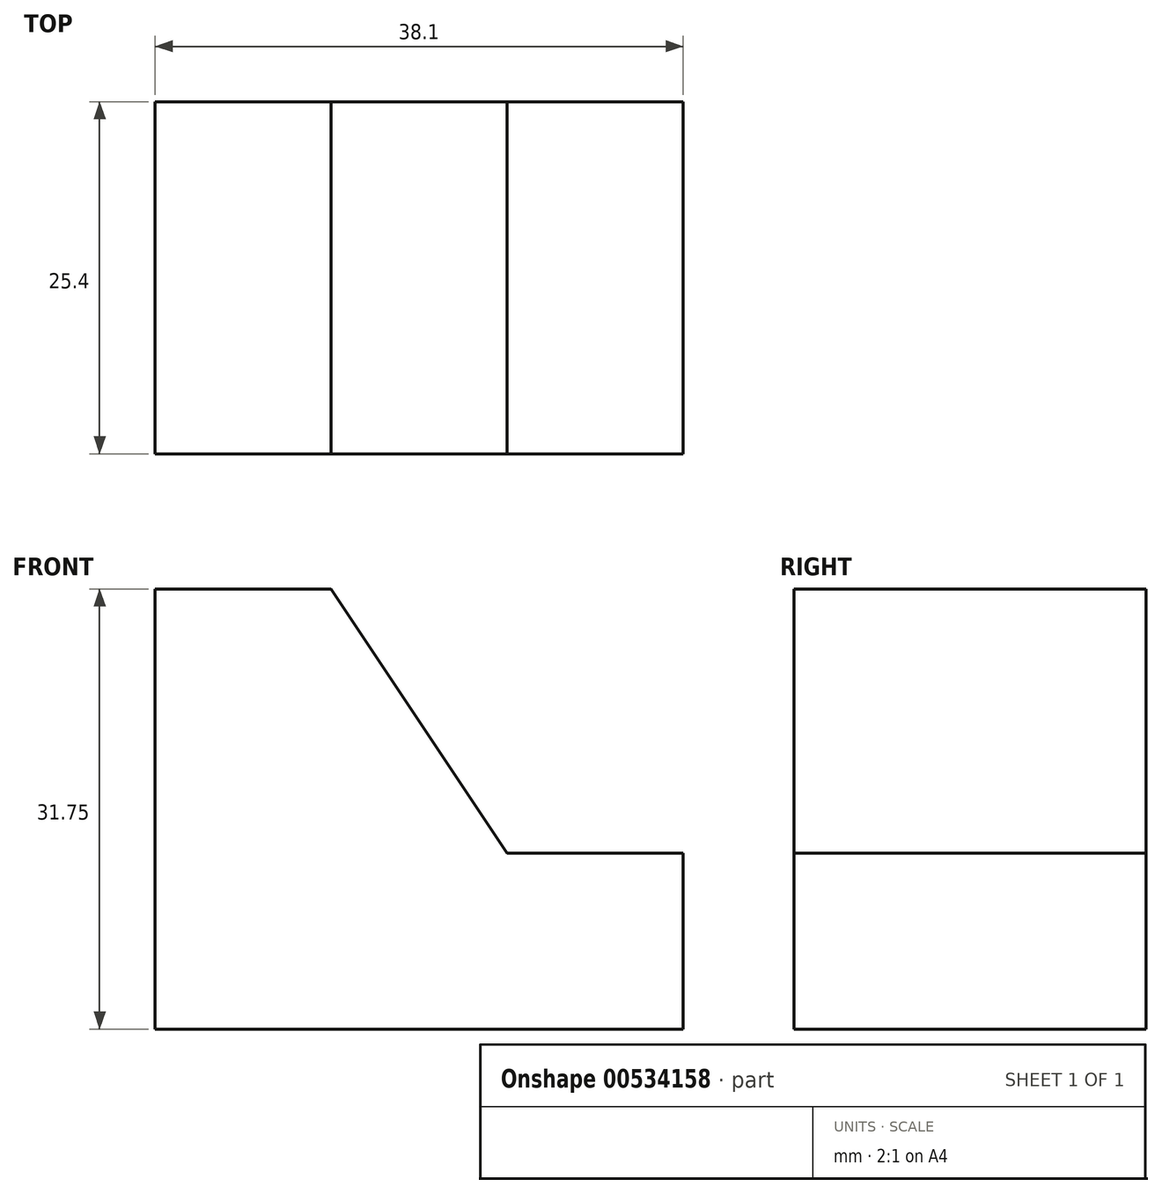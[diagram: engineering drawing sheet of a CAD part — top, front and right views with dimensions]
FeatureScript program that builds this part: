
annotation { "Feature Type Name" : "Feature", "Feature Type Description" : "" }
export const myFeature = defineFeature(function(context is Context, id is Id, definition is map)
    precondition{}
    {
        {
            var Q0;
            Q0=qCreatedBy(makeId("Front.planeOp"),FACE);
            var sketch = newSketch(context, id + "F0", { "sketchPlane" : qUnion([Q0])});
            skLineSegment(sketch, "E0", {"start": v(0, 0) * mm, "end": v(38.1, 0) * mm});
            skLineSegment(sketch, "E1", {"start": v(0, 0) * mm, "end": v(0, 31.75) * mm});
            skLineSegment(sketch, "E2", {"start": v(0, 31.75) * mm, "end": v(12.7, 31.75) * mm});
            skLineSegment(sketch, "E3", {"start": v(38.1, 0) * mm, "end": v(38.1, 12.7) * mm});
            skLineSegment(sketch, "E4", {"start": v(38.1, 12.7) * mm, "end": v(25.4, 12.7) * mm});
            skLineSegment(sketch, "E5", {"start": v(12.7, 31.75) * mm, "end": v(25.4, 12.7) * mm});
            skSolve(sketch);
        }
        {
            var Q0;
            Q0 = qSketchRegion(id + "F0", true);
            extrude(context, id + "F1", {"entities" : qUnion([Q0]), "depth" : 25.4 * mm, "offsetDistance" : 25.4 * mm});
        }
    });
